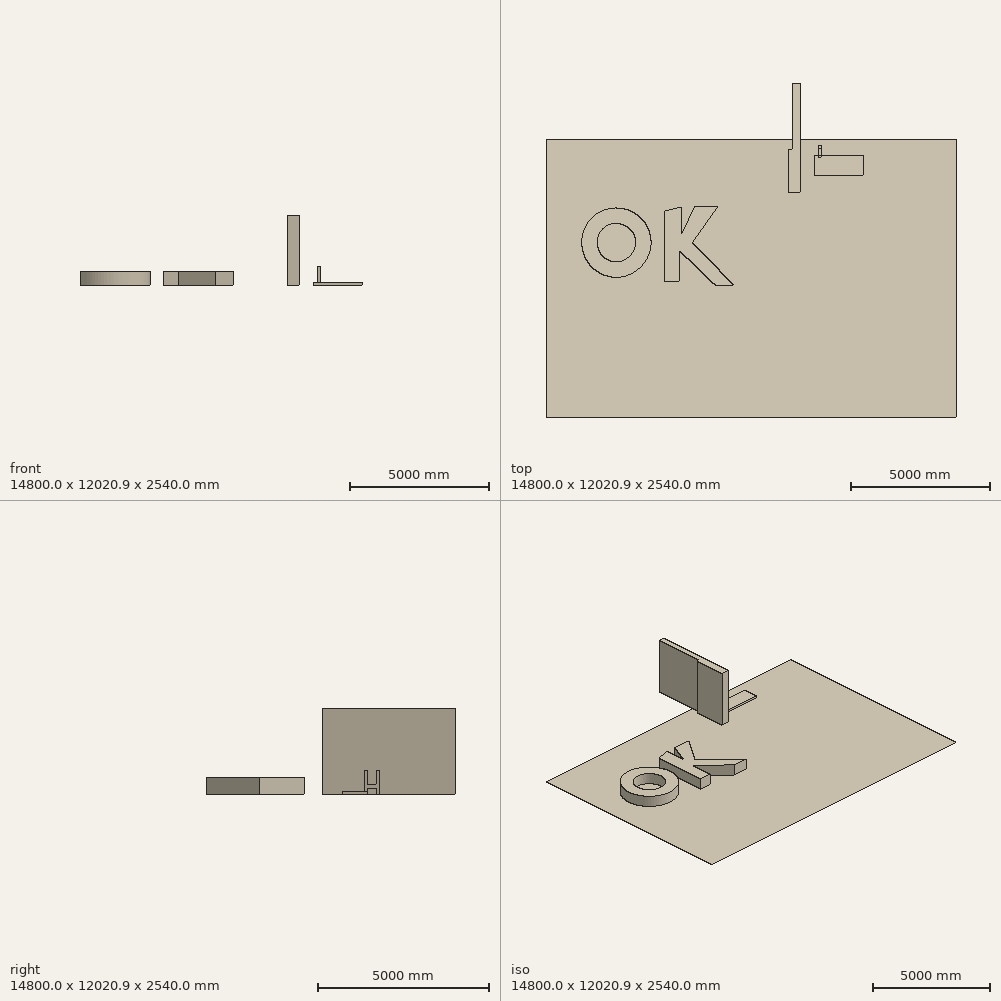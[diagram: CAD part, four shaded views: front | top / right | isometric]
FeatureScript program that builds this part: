
annotation { "Feature Type Name" : "Feature", "Feature Type Description" : "" }
export const myFeature = defineFeature(function(context is Context, id is Id, definition is map)
    precondition{}
    {
        {
            var Q0;
            Q0=qCreatedBy(makeId("Top.planeOp"),FACE);
            var sketch = newSketch(context, id + "F0", { "sketchPlane" : qUnion([Q0])});
            skLineSegment(sketch, "E0", {"start": v(-1084.26, -560.28) * mm, "end": v(-674.26, -560.28) * mm});
            skLineSegment(sketch, "E1", {"start": v(-1084.26, -560.28) * mm, "end": v(-1084.26, 959.72) * mm});
            skLineSegment(sketch, "E2", {"start": v(-1084.26, 959.72) * mm, "end": v(-954.26, 959.72) * mm});
            skLineSegment(sketch, "E3", {"start": v(-954.26, 959.72) * mm, "end": v(-954.26, 3339.72) * mm});
            skLineSegment(sketch, "E4", {"start": v(-954.26, 3339.72) * mm, "end": v(-674.26, 3339.72) * mm});
            skLineSegment(sketch, "E5", {"start": v(-674.26, 3339.72) * mm, "end": v(-674.26, -560.28) * mm});
            skSolve(sketch);
        }
        {
            var Q0;
            Q0 = qSketchRegion(id + "F0", true);
            extrude(context, id + "F1", {"entities" : qUnion([Q0]), "depth" : 2540 * mm});
        }
        {
            var Q0;
            Q0=qCreatedBy(makeId("Top.planeOp"),FACE);
            var sketch = newSketch(context, id + "F2", { "sketchPlane" : qUnion([Q0])});
            skLineSegment(sketch, "E6.bottom", {"start": v(-138.49, 749.7) * mm, "end": v(1611.51, 749.7) * mm});
            skLineSegment(sketch, "E6.top", {"start": v(-138.49, 39.7) * mm, "end": v(1611.51, 39.7) * mm});
            skLineSegment(sketch, "E6.left", {"start": v(-138.49, 749.7) * mm, "end": v(-138.49, 39.7) * mm});
            skLineSegment(sketch, "E6.right", {"start": v(1611.51, 749.7) * mm, "end": v(1611.51, 39.7) * mm});
            skSolve(sketch);
        }
        {
            var Q0;
            Q0 = qSketchRegion(id + "F2", true);
            extrude(context, id + "F3", {"entities" : qUnion([Q0]), "depth" : 100 * mm});
        }
        {
            var Q0;
            Q0=qCreatedBy(makeId("Right.planeOp"),FACE);
            var sketch = newSketch(context, id + "F4", { "sketchPlane" : qUnion([Q0])});
            skLineSegment(sketch, "E7.bottom", {"start": v(671.2, 700) * mm, "end": v(771.2, 700) * mm});
            skLineSegment(sketch, "E7.top", {"start": v(671.2, 0) * mm, "end": v(771.2, 0) * mm});
            skLineSegment(sketch, "E7.left", {"start": v(671.2, 700) * mm, "end": v(671.2, 0) * mm});
            skLineSegment(sketch, "E7.right", {"start": v(771.2, 700) * mm, "end": v(771.2, 0) * mm});
            skLineSegment(sketch, "E8.bottom", {"start": v(771.2, 290.05) * mm, "end": v(1022.7, 290.05) * mm});
            skLineSegment(sketch, "E8.top", {"start": v(771.2, 190.05) * mm, "end": v(1022.7, 190.05) * mm});
            skLineSegment(sketch, "E8.left", {"start": v(771.2, 290.05) * mm, "end": v(771.2, 190.05) * mm});
            skLineSegment(sketch, "E8.right", {"start": v(1022.7, 290.05) * mm, "end": v(1022.7, 190.05) * mm});
            skLineSegment(sketch, "E9.bottom", {"start": v(1022.7, 700) * mm, "end": v(1122.7, 700) * mm});
            skLineSegment(sketch, "E9.top", {"start": v(1022.7, 0) * mm, "end": v(1122.7, 0) * mm});
            skLineSegment(sketch, "E9.left", {"start": v(1022.7, 700) * mm, "end": v(1022.7, 0) * mm});
            skLineSegment(sketch, "E9.right", {"start": v(1122.7, 700) * mm, "end": v(1122.7, 0) * mm});
            skSolve(sketch);
        }
        {
            var Q0;
            Q0 = qSketchRegion(id + "F4", true);
            extrude(context, id + "F5", {"entities" : qUnion([Q0]), "depth" : 100 * mm});
        }
        {
            var Q0;
            Q0=qCreatedBy(makeId("Top.planeOp"),FACE);
            var sketch = newSketch(context, id + "F6", { "sketchPlane" : qUnion([Q0])});
            skLineSegment(sketch, "E10.bottom", {"start": v(-9829.8, -8681.18) * mm, "end": v(4970.2, -8681.18) * mm});
            skLineSegment(sketch, "E10.top", {"start": v(-9829.8, 1318.82) * mm, "end": v(4970.2, 1318.82) * mm});
            skLineSegment(sketch, "E10.left", {"start": v(-9829.8, -8681.18) * mm, "end": v(-9829.8, 1318.82) * mm});
            skLineSegment(sketch, "E10.right", {"start": v(4970.2, -8681.18) * mm, "end": v(4970.2, 1318.82) * mm});
            skSolve(sketch);
        }
        {
            var Q0;
            Q0=makeQuery(id+"F6.imprint","IMPRINT",FACE,{"disambiguationData":[TD([[makeQuery(id+"F6.imprint","IMPRINT",EDGE,{"derivedFrom":sQuery(id+"F6.wireOp",EDGE,"E10.bottom")}),1.0]])]});
            extrude(context, id + "F7", {"entities" : qUnion([Q0]), "depth" : 1 * mm});
        }
        {
            var Q0;
            Q0=makeQuery(id+"F7.opExtrude","CAP_FACE",FACE,{"disambiguationData":[OSD([sQuery(id+"F6.wireOp",EDGE,"E10.bottom"),sQuery(id+"F6.wireOp",EDGE,"E10.top"),sQuery(id+"F6.wireOp",EDGE,"E10.left"),sQuery(id+"F6.wireOp",EDGE,"E10.right")])],"isStart":false});
            var sketch = newSketch(context, id + "F8", { "sketchPlane" : qUnion([Q0])});
            skCircle(sketch, "E11", {"center": v(-7305.18, -2387.84) * mm, "radius": 1252.17 * mm});
            skCircle(sketch, "E12", {"center": v(-7305.18, -2387.84) * mm, "radius": 693.69 * mm});
            skLineSegment(sketch, "E13", {"start": v(-5587.72, -1259.23) * mm, "end": v(-5587.72, -3780.49) * mm});
            skLineSegment(sketch, "E14", {"start": v(-5587.72, -3780.49) * mm, "end": v(-5029.3, -3780.49) * mm});
            skLineSegment(sketch, "E15", {"start": v(-5029.3, -3780.49) * mm, "end": v(-5029.3, -2681.3) * mm});
            skLineSegment(sketch, "E16", {"start": v(-5029.3, -2681.3) * mm, "end": v(-3708.83, -3951.62) * mm});
            skLineSegment(sketch, "E17", {"start": v(-3708.83, -3951.62) * mm, "end": v(-3032.75, -3951.62) * mm});
            skLineSegment(sketch, "E18", {"start": v(-3032.75, -3951.62) * mm, "end": v(-4565.95, -2399.6) * mm});
            skLineSegment(sketch, "E19", {"start": v(-4565.95, -2399.6) * mm, "end": v(-3636.64, -1095.11) * mm});
            skLineSegment(sketch, "E20", {"start": v(-3636.64, -1095.11) * mm, "end": v(-4481.68, -1095.11) * mm});
            skLineSegment(sketch, "E21", {"start": v(-4481.68, -1095.11) * mm, "end": v(-4949.35, -2094.82) * mm});
            skLineSegment(sketch, "E22", {"start": v(-4949.35, -2094.82) * mm, "end": v(-4949.35, -1099.34) * mm});
            skLineSegment(sketch, "E23", {"start": v(-4949.35, -1099.34) * mm, "end": v(-5587.72, -1259.23) * mm});
            skSolve(sketch);
        }
        {
            var Q0;
            Q0 = qSketchRegion(id + "F8", true);
            extrude(context, id + "F9", {"entities" : qUnion([Q0]), "depth" : 500 * mm});
        }
    });
